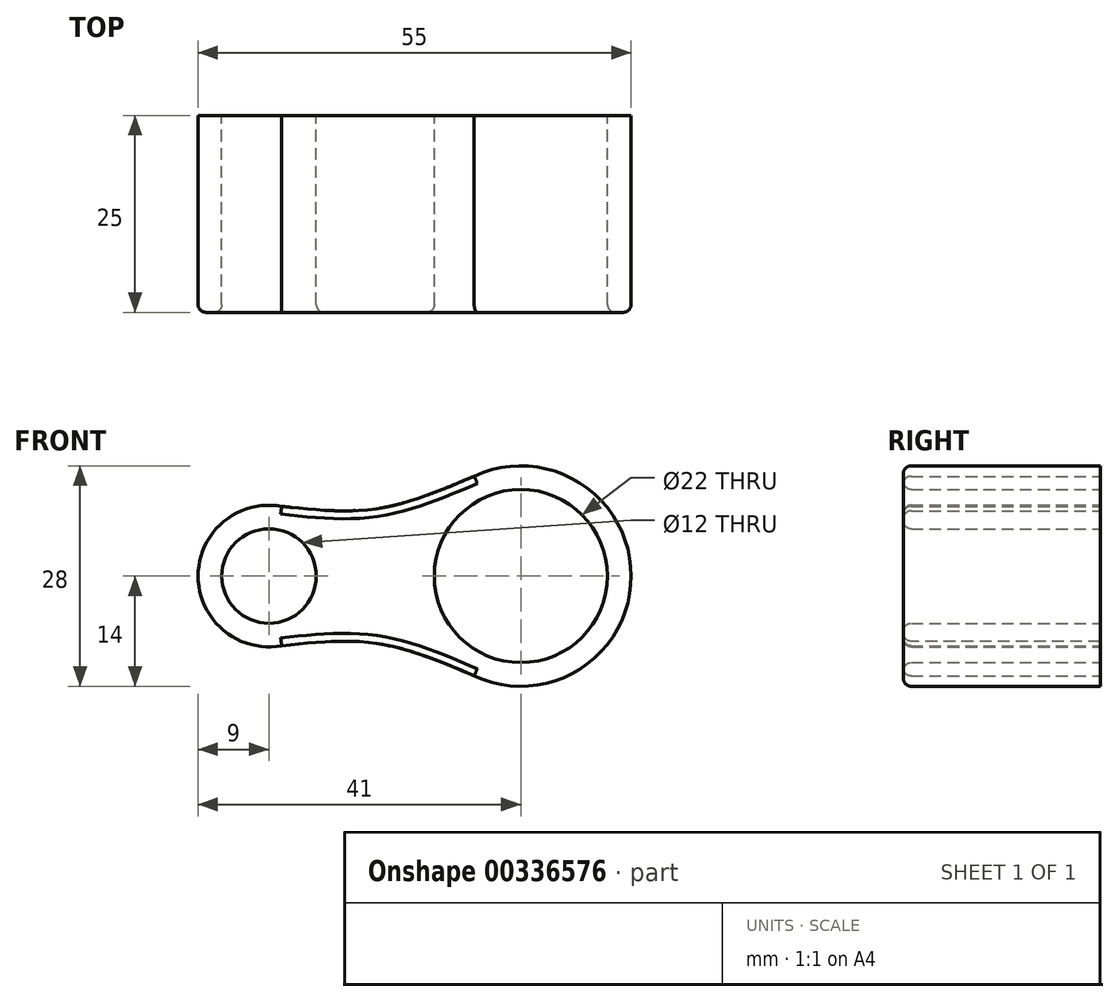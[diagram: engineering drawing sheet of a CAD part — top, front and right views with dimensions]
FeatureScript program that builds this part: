
annotation { "Feature Type Name" : "Feature", "Feature Type Description" : "" }
export const myFeature = defineFeature(function(context is Context, id is Id, definition is map)
    precondition{}
    {
        {
            var Q0;
            Q0=qCreatedBy(makeId("Front.planeOp"),FACE);
            var sketch = newSketch(context, id + "F0", { "sketchPlane" : qUnion([Q0])});
            skCircle(sketch, "E0", {"center": v(0, 0) * mm, "radius": 14 * mm});
            skCircle(sketch, "E1", {"center": v(0, 0) * mm, "radius": 11 * mm});
            skCircle(sketch, "E2", {"center": v(-32, 0) * mm, "radius": 9 * mm});
            skCircle(sketch, "E3", {"center": v(-32, 0) * mm, "radius": 6 * mm});
            skFitSpline(sketch, "E4", {"points": [v(-30.38, 8.85) * mm, v(-18.21, 8.58) * mm, v(-5.93, 12.68) * mm], "startDerivative": vector(24.84, -2.68) * mm, "endDerivative": vector(24.05, 10.27) * mm});
            skLineSegment(sketch, "E5", {"start": v(-32, 0) * mm, "end": v(0, 0) * mm});
            skFitSpline(sketch, "E6.MirrorCS", {"points": [v(-30.38, -8.85) * mm, v(-18.21, -8.58) * mm, v(-5.93, -12.68) * mm], "startDerivative": vector(24.84, 2.68) * mm, "endDerivative": vector(24.05, -10.27) * mm});
            skSolve(sketch);
        }
        {
            var Q0;
            Q0 = qSketchRegion(id + "F0", true);
            extrude(context, id + "F1", {"entities" : qUnion([Q0]), "depth" : 25 * mm});
        }
        {
            var Q0;
            Q0=makeQuery(id+"F1.opExtrude","CAP_EDGE",EDGE,{"disambiguationData":[OSD([sQuery(id+"F0.wireOp",EDGE,"E1")])],"isStart":false});
            var Q1;
            Q1=makeQuery(id+"F1.opExtrude","CAP_EDGE",EDGE,{"disambiguationData":[OSD([sQuery(id+"F0.wireOp",EDGE,"E3")])],"isStart":false});
            var Q2;
            Q2=makeQuery(id+"F1.opExtrude","CAP_EDGE",EDGE,{"disambiguationData":[OSD([sQuery(id+"F0.wireOp",EDGE,"E2")])],"isStart":false});
            var Q3;
            Q3=makeQuery(id+"F1.opExtrude","CAP_EDGE",EDGE,{"disambiguationData":[OSD([sQuery(id+"F0.wireOp",EDGE,"E0")])],"isStart":false});
            fillet(context, id + "F2", {"entities" : qUnion([Q0, Q1, Q2, Q3]), "radius" : 1 * mm, "tangentPropagation" : true, "allowEdgeOverflow" : false});
        }
    });
